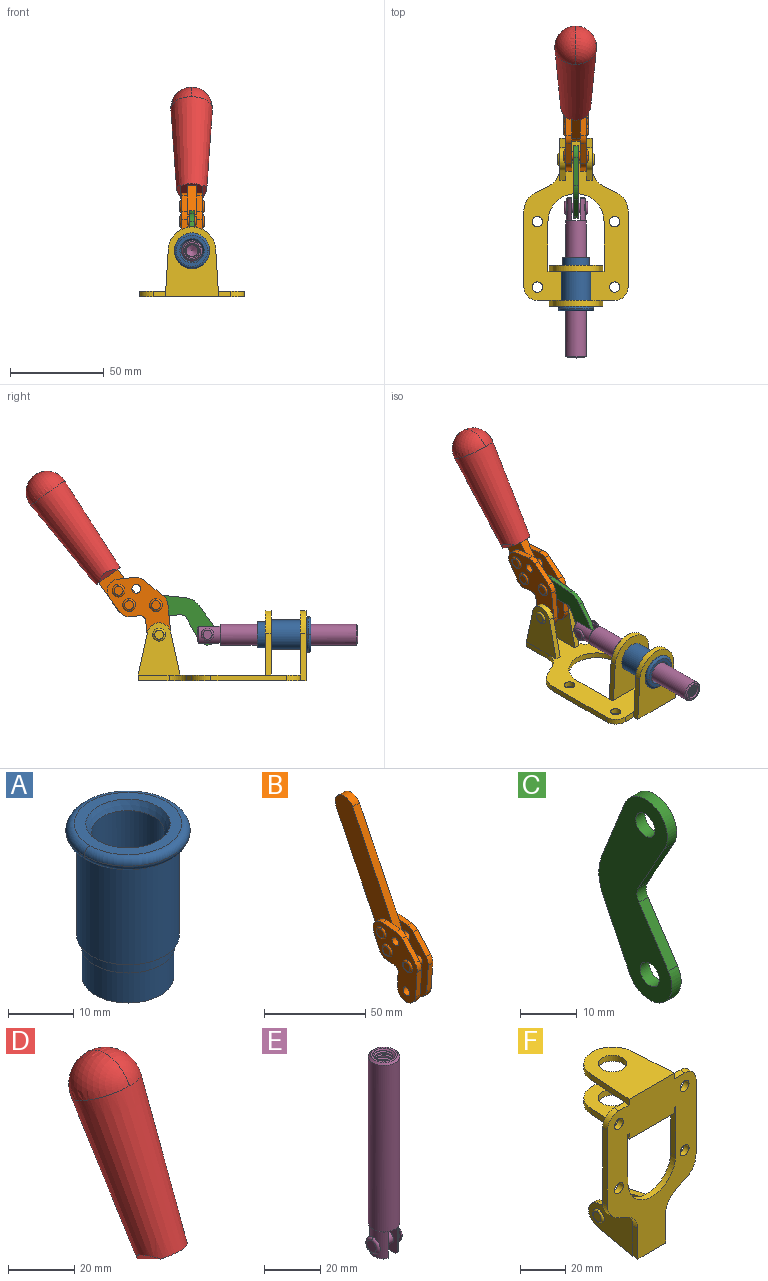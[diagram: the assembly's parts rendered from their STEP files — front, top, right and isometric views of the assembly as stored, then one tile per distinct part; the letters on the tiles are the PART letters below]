
ASSEMBLY  parts=6 mates=6
PART A: 15 faces, bbox 20.6x20.6x28.7 mm
  f0: torus R=8.26mm, axis (0,0,1), area 56.8mm2, adj f1,f10,f12
  f1: torus R=8.26mm, axis (0,0,1), area 56.8mm2, adj f0,f6,f13
  f2: cylinder r=5.59mm len=25.91mm, axis (0,0,1), area 909.6mm2, adj f3,f4
  f3: cone r=6.86mm half-angle=45deg, axis (0,0,-1), area 70.2mm2, adj f2,f14
  f4: cone r=6.47mm half-angle=30deg, axis (0,0,1), area 66.7mm2, adj f2,f13
  f5: cylinder r=7.04mm len=14.07mm, axis (0,0,1), area 252.6mm2, adj f11,f14
  f6: torus R=8.26mm, axis (0,0,1), area 56.8mm2, adj f1,f12,f13
  f7: cylinder r=7.16mm len=14.33mm, axis (0,0,1), area 91.5mm2, adj f9,f11
  f8: cylinder r=7.86mm len=18.42mm, axis (0,0,1), area 909.6mm2, adj f9,f10
  f9: plane 15.72x15.72mm, normal (0,0,-1), area 33mm2, adj f7,f8
  f10: plane 16.51x16.51mm, normal (0,0,-1), area 19.9mm2, adj f0,f8,f12
  f11: plane 14.33x14.33mm, normal (0,0,-1), area 5.7mm2, adj f5,f7
  f12: torus R=8.26mm, axis (0,0,1), area 56.8mm2, adj f0,f6,f10
  f13: plane 16.51x16.51mm, normal (0,0,1), area 82.7mm2, adj f1,f4,f6
  f14: plane 14.07x14.07mm, normal (0,0,-1), area 7.8mm2, adj f3,f5
PART B: 59 faces, bbox 12.9x60.2x99.6 mm
  f0: torus R=2.39mm, axis (-1,0,0), area 14.9mm2, adj f20,f43,f51
  f1: torus R=2.39mm, axis (-1,0,0), area 14.9mm2, adj f19,f42,f51
  f2: torus R=2.39mm, axis (-1,0,0), area 14.9mm2, adj f18,f35,f51
  f3: torus R=2.39mm, axis (-1,0,0), area 14.9mm2, adj f14,f17,f23
  f4: torus R=2.39mm, axis (-1,0,0), area 14.9mm2, adj f13,f16,f23
  f5: torus R=2.39mm, axis (-1,0,0), area 14.9mm2, adj f12,f15,f23
  f6: cylinder r=2.39mm len=4.78mm, axis (1,0,0), area 46.5mm2, adj f48,f50,f51
  f7: cylinder r=2.39mm len=4.78mm, axis (1,0,0), area 46.5mm2, adj f50,f51
  f8: cylinder r=6.35mm len=12.68mm, axis (1,0,0), area 61.8mm2, adj f38,f39,f50,f51
  f9: cylinder r=2.39mm len=4.78mm, axis (-1,0,0), area 70.5mm2, adj f46,f50
  f10: cylinder r=2.39mm len=4.78mm, axis (-1,0,0), area 46.5mm2, adj f23,f45,f46
  f11: cylinder r=2.39mm len=4.78mm, axis (-1,0,0), area 46.5mm2, adj f23,f46
  f12: plane 4.78x4.78mm, normal (1,0,0), area 17.9mm2, adj f5,f15
  f13: plane 4.78x4.78mm, normal (1,0,0), area 17.9mm2, adj f4,f16
  f14: plane 4.78x4.78mm, normal (1,0,0), area 17.9mm2, adj f3,f17
  f15: torus R=2.39mm, axis (-1,0,0), area 14.9mm2, adj f5,f12,f23
  f16: torus R=2.39mm, axis (-1,0,0), area 14.9mm2, adj f4,f13,f23
  f17: torus R=2.39mm, axis (-1,0,0), area 14.9mm2, adj f3,f14,f23
  f18: plane 4.78x4.78mm, normal (-1,0,0), area 17.9mm2, adj f2,f35
  f19: plane 4.78x4.78mm, normal (-1,0,0), area 17.9mm2, adj f1,f42
  f20: plane 4.78x4.78mm, normal (-1,0,0), area 17.9mm2, adj f0,f43
  f21: plane 2.26x0.2mm, normal (1,0,0), area 0.2mm2, adj f31,f44
  f22: plane 2.26x0.2mm, normal (-1,0,0), area 0.2mm2, adj f41,f44
  f23: plane 39.37x30.77mm, normal (1,0,0), area 565.5mm2, adj f3,f4,f5,f10,f11,f15,f16,f17
  f24: cylinder r=6.1mm len=4.15mm, axis (-1,0,0), area 14.7mm2, adj f23,f25,f32,f46
  f25: plane 10.25x9.01mm, normal (0,-0.75,0.66), area 42.3mm2, adj f23,f24,f26,f46
  f26: cylinder r=6.35mm len=4.64mm, axis (-1,0,0), area 15.6mm2, adj f23,f25,f27,f46
  f27: plane 15.84x3.1mm, normal (0,-1,-0.07), area 49.2mm2, adj f23,f26,f28,f46
  f28: cylinder r=6.35mm len=12.68mm, axis (-1,0,0), area 61.8mm2, adj f23,f27,f29,f46
  f29: plane 8.11x3.1mm, normal (0,1,0.07), area 25.2mm2, adj f23,f28,f30,f46
  f30: cylinder r=3.05mm len=3.25mm, axis (-1,0,0), area 14.8mm2, adj f23,f29,f31,f46
  f31: plane 5.99x3.1mm, normal (0,0.07,-1), area 18.6mm2, adj f21,f23,f30,f44,f46
  f32: plane 9.5x3.1mm, normal (0,-0.07,1), area 29.5mm2, adj f23,f24,f33,f46,f47
  f33: cylinder r=6.1mm len=8.63mm, axis (-1,0,0), area 39.1mm2, adj f23,f32,f34,f47
  f34: plane 8.65x3.96mm, normal (0,0.91,-0.42), area 29.5mm2, adj f23,f33,f44,f47
  f35: torus R=2.39mm, axis (-1,0,0), area 14.9mm2, adj f2,f18,f51
  f36: plane 10.25x9.01mm, normal (0,-0.75,0.66), area 42.3mm2, adj f37,f49,f50,f51
  f37: cylinder r=6.35mm len=4.64mm, axis (1,0,0), area 15.6mm2, adj f36,f38,f50,f51
  f38: plane 15.84x3.1mm, normal (0,-1,-0.07), area 49.2mm2, adj f8,f37,f50,f51
  f39: plane 8.11x3.1mm, normal (0,1,0.07), area 25.2mm2, adj f8,f40,f50,f51
  f40: cylinder r=3.05mm len=3.25mm, axis (1,0,0), area 14.8mm2, adj f39,f41,f50,f51
  f41: plane 5.99x3.1mm, normal (0,0.07,-1), area 18.6mm2, adj f22,f40,f44,f50,f51
  f42: torus R=2.39mm, axis (-1,0,0), area 14.9mm2, adj f1,f19,f51
  f43: torus R=2.39mm, axis (-1,0,0), area 14.9mm2, adj f0,f20,f51
  f44: cylinder r=6.35mm len=12.12mm, axis (-1,0,0), area 128.9mm2, adj f21,f22,f23,f31,f34,f41,f46,f47
  f45: plane 2.65x1.35mm, normal (1,0,0), area 1mm2, adj f10,f55
  f46: plane 39.08x20.42mm, normal (-1,0,0), area 412.5mm2, adj f9,f10,f11,f24,f25,f26,f27,f28
  f47: plane 77.62x39.82mm, normal (1,0,0), area 850mm2, adj f32,f33,f34,f44,f53,f54,f55
  f48: plane 2.65x1.35mm, normal (-1,0,0), area 1mm2, adj f6,f55
  f49: cylinder r=6.1mm len=4.15mm, axis (1,0,0), area 14.7mm2, adj f36,f50,f51,f56
  f50: plane 39.08x20.42mm, normal (1,0,0), area 412.5mm2, adj f6,f7,f8,f9,f36,f37,f38,f39
  f51: plane 39.37x30.77mm, normal (-1,0,0), area 565.5mm2, adj f0,f1,f2,f6,f7,f8,f35,f36
  f52: plane 8.65x3.96mm, normal (0,0.91,-0.42), area 29.5mm2, adj f44,f51,f57,f58
  f53: plane 68.49x33.4mm, normal (0,0.9,-0.44), area 358.1mm2, adj f44,f47,f54,f58
  f54: cylinder r=6.35mm len=12.06mm, axis (1,0,0), area 93.7mm2, adj f47,f53,f55,f58
  f55: plane 68.49x33.4mm, normal (0,-0.9,0.44), area 358.1mm2, adj f44,f45,f46,f47,f48,f50,f54,f58
  f56: plane 9.5x3.1mm, normal (0,-0.07,1), area 29.5mm2, adj f49,f50,f51,f57,f58
  f57: cylinder r=6.1mm len=8.63mm, axis (1,0,0), area 39.1mm2, adj f51,f52,f56,f58
  f58: plane 77.62x39.82mm, normal (-1,0,0), area 850mm2, adj f44,f52,f53,f54,f55,f56,f57
PART C: 12 faces, bbox 2.3x18.2x42.8 mm
  f0: cylinder r=2.4mm len=4.8mm, axis (1,0,0), area 34.9mm2, adj f4,f11
  f1: cylinder r=10.41mm len=8.47mm, axis (1,0,0), area 20.2mm2, adj f4,f9,f10,f11
  f2: cylinder r=3.05mm len=3.16mm, axis (1,0,0), area 7.7mm2, adj f4,f6,f7,f11
  f3: cylinder r=2.4mm len=4.8mm, axis (1,0,0), area 34.9mm2, adj f4,f11
  f4: plane 42.81x18.23mm, normal (-1,0,0), area 414.1mm2, adj f0,f1,f2,f3,f5,f6,f7,f8
  f5: cylinder r=5.54mm len=10.67mm, axis (1,0,0), area 41.8mm2, adj f4,f6,f10,f11
  f6: plane 11.66x6.53mm, normal (0,-0.87,-0.49), area 30.9mm2, adj f2,f4,f5,f11
  f7: plane 11.17x7.33mm, normal (0,-0.84,0.55), area 30.9mm2, adj f2,f4,f8,f11
  f8: cylinder r=5.54mm len=10.51mm, axis (1,0,0), area 41.8mm2, adj f4,f7,f9,f11
  f9: plane 13.67x6.67mm, normal (0,0.9,-0.44), area 35.1mm2, adj f1,f4,f8,f11
  f10: plane 14.1x5.7mm, normal (0,0.93,0.37), area 35.1mm2, adj f1,f4,f5,f11
  f11: plane 42.81x18.23mm, normal (1,0,0), area 414.1mm2, adj f0,f1,f2,f3,f5,f6,f7,f8
PART D: 11 faces, bbox 22.3x42.6x64.5 mm
  f0: sphere r=11.13mm, area 411.4mm2, adj f1,f8
  f1: cone r=11.11mm half-angle=3.3deg, axis (0,0.44,0.9), area 3251.8mm2, adj f0,f7,f8,f9,f10
  f2: cylinder r=6.16mm len=11.7mm, axis (1,0,0), area 89.5mm2, adj f3,f4,f5,f6
  f3: plane 60.23x36.75mm, normal (-1,0,0), area 763.6mm2, adj f2,f4,f6,f10
  f4: plane 51.37x25.05mm, normal (0,0.9,-0.44), area 264.2mm2, adj f2,f3,f5,f10
  f5: plane 60.23x36.75mm, normal (1,0,0), area 763.6mm2, adj f2,f4,f6,f10
  f6: plane 51.37x25.05mm, normal (0,-0.9,0.44), area 264.2mm2, adj f2,f3,f5,f10
  f7: plane 9.95x5.95mm, normal (0.71,-0.31,-0.64), area 25.8mm2, adj f1,f10
  f8: sphere r=11.13mm, area 411.4mm2, adj f0,f1
  f9: plane 9.95x5.95mm, normal (-0.71,-0.31,-0.64), area 25.8mm2, adj f1,f10
  f10: plane 14.27x11.38mm, normal (0,-0.44,-0.9), area 106.7mm2, adj f1,f3,f4,f5,f6,f7,f9
PART E: 48 faces, bbox 12.6x11.1x86.1 mm
  f0: torus R=2.41mm, axis (-1,0,0), area 15mm2, adj f30,f32,f34
  f1: torus R=2.41mm, axis (-1,0,0), area 15mm2, adj f29,f31,f33
  f2: cylinder r=5.54mm len=72.39mm, axis (0,0,1), area 2518.5mm2, adj f3,f4,f42,f43
  f3: cone r=5.54mm half-angle=45deg, axis (0,0,1), area 7.6mm2, adj f2,f5,f41
  f4: cone r=5.54mm half-angle=45deg, axis (0,0,-1), area 34.9mm2, adj f2,f39
  f5: cylinder r=5.08mm len=11.48mm, axis (0,0,1), area 108.3mm2, adj f3,f7,f8,f41
  f6: cylinder r=2.41mm len=4.83mm, axis (-1,0,0), area 71.2mm2, adj f40,f41
  f7: cylinder r=2.41mm len=4.83mm, axis (-1,0,0), area 7.6mm2, adj f5,f34
  f8: cone r=5.08mm half-angle=45deg, axis (0,0,1), area 10.6mm2, adj f5,f37,f41
  f9: cone r=3.98mm half-angle=45deg, axis (0,0,1), area 17.6mm2, adj f27,f39,f45,f46,f47
  f10: cylinder r=2.41mm len=4.83mm, axis (-1,0,0), area 7.6mm2, adj f33,f38
  f11: cylinder r=3.2mm len=6.4mm, axis (0,0,1), area 78.4mm2, adj f12,f28,f44,f45,f47
  f12: cylinder r=3.2mm len=6.4mm, axis (0,0,1), area 10.5mm2, adj f11,f13,f45,f47
  f13: cylinder r=3.2mm len=6.4mm, axis (0,0,1), area 10.5mm2, adj f12,f14,f45,f47
  f14: cylinder r=3.2mm len=6.4mm, axis (0,0,1), area 10.5mm2, adj f13,f15,f45,f47
  f15: cylinder r=3.2mm len=6.4mm, axis (0,0,1), area 10.5mm2, adj f14,f16,f45,f47
  f16: cylinder r=3.2mm len=6.4mm, axis (0,0,1), area 10.5mm2, adj f15,f17,f45,f47
  f17: cylinder r=3.2mm len=6.4mm, axis (0,0,1), area 10.5mm2, adj f16,f18,f45,f47
  f18: cylinder r=3.2mm len=6.4mm, axis (0,0,1), area 10.5mm2, adj f17,f19,f45,f47
  f19: cylinder r=3.2mm len=6.4mm, axis (0,0,1), area 10.5mm2, adj f18,f20,f45,f47
  f20: cylinder r=3.2mm len=6.4mm, axis (0,0,1), area 10.5mm2, adj f19,f21,f45,f47
  f21: cylinder r=3.2mm len=6.4mm, axis (0,0,1), area 10.5mm2, adj f20,f22,f45,f47
  f22: cylinder r=3.2mm len=6.4mm, axis (0,0,1), area 10.5mm2, adj f21,f23,f45,f47
  f23: cylinder r=3.2mm len=6.4mm, axis (0,0,1), area 10.5mm2, adj f22,f24,f45,f47
  f24: cylinder r=3.2mm len=6.4mm, axis (0,0,1), area 10.5mm2, adj f23,f25,f45,f47
  f25: cylinder r=3.2mm len=6.4mm, axis (0,0,1), area 10.5mm2, adj f24,f26,f45,f47
  f26: cylinder r=3.2mm len=6.4mm, axis (0,0,1), area 10.5mm2, adj f25,f27,f45,f47
  f27: cylinder r=3.2mm len=6.4mm, axis (0,0,1), area 7.4mm2, adj f9,f26,f45,f47
  f28: cone r=3.2mm half-angle=60deg, axis (0,0,1), area 37.2mm2, adj f11
  f29: plane 4.83x4.83mm, normal (-1,0,0), area 18.3mm2, adj f1,f31
  f30: plane 4.83x4.83mm, normal (1,0,0), area 18.3mm2, adj f0,f32
  f31: torus R=2.41mm, axis (-1,0,0), area 15mm2, adj f1,f29,f33
  f32: torus R=2.41mm, axis (-1,0,0), area 15mm2, adj f0,f30,f34
  f33: plane 6.83x6.83mm, normal (1,0,0), area 18.3mm2, adj f1,f10,f31
  f34: plane 6.83x6.83mm, normal (-1,0,0), area 18.3mm2, adj f0,f7,f32
  f35: cone r=5.08mm half-angle=45deg, axis (0,0,1), area 10.6mm2, adj f36,f38,f40
  f36: plane 7.25x1.97mm, normal (0,0,-1), area 10mm2, adj f35,f40
  f37: plane 7.25x1.97mm, normal (0,0,-1), area 10mm2, adj f8,f41
  f38: cylinder r=5.08mm len=11.48mm, axis (0,0,1), area 108.3mm2, adj f10,f35,f40,f42
  f39: plane 9.55x9.55mm, normal (0,0,1), area 22mm2, adj f4,f9
  f40: plane 12.76x10.09mm, normal (1,0,0), area 95.7mm2, adj f6,f35,f36,f38,f42,f43
  f41: plane 12.76x10.09mm, normal (-1,0,0), area 95.7mm2, adj f3,f5,f6,f8,f37,f43
  f42: cone r=5.54mm half-angle=45deg, axis (0,0,1), area 7.6mm2, adj f2,f38,f40
  f43: plane 11.07x4.7mm, normal (0,0,-1), area 50.4mm2, adj f2,f40,f41
  f44: plane 0.89x0.62mm, normal (-1,0,0), area 0.3mm2, adj f11,f45,f46,f47
  f45: bspline ~24.8x7.63mm, area 266.6mm2, adj f9,f11,f12,f13,f14,f15,f16,f17
  f46: bspline ~24.87x7.63mm, area 73.6mm2, adj f9,f44,f45,f47
  f47: bspline ~24.98x7.63mm, area 272.5mm2, adj f9,f11,f12,f13,f14,f15,f16,f17
PART F: 55 faces, bbox 55.7x37.4x89.8 mm
  f0: torus R=2.41mm, axis (-1,0,0), area 15mm2, adj f11,f15,f25
  f1: torus R=2.41mm, axis (-1,0,0), area 15mm2, adj f10,f12,f22
  f2: cylinder r=2.78mm len=5.56mm, axis (0,-1,0), area 54.2mm2, adj f30,f54
  f3: cylinder r=14.99mm len=29.97mm, axis (0,-1,0), area 145.9mm2, adj f30,f49,f53,f54
  f4: cylinder r=2.78mm len=5.56mm, axis (0,-1,0), area 54.2mm2, adj f30,f54
  f5: cylinder r=2.78mm len=5.56mm, axis (0,-1,0), area 54.2mm2, adj f30,f54
  f6: cylinder r=2.78mm len=5.56mm, axis (0,-1,0), area 54.2mm2, adj f30,f54
  f7: cylinder r=6.35mm len=12.7mm, axis (0,0,1), area 123.6mm2, adj f27,f51
  f8: cylinder r=6.35mm len=12.7mm, axis (0,0,-1), area 124.7mm2, adj f21,f35
  f9: cylinder r=2.41mm len=11.18mm, axis (-1,0,0), area 169.4mm2, adj f16,f19
  f10: plane 4.83x4.83mm, normal (1,0,0), area 18.3mm2, adj f1,f12
  f11: plane 4.83x4.83mm, normal (-1,0,0), area 18.3mm2, adj f0,f15
  f12: torus R=2.41mm, axis (-1,0,0), area 15mm2, adj f1,f10,f22
  f13: cylinder r=6.35mm len=12.41mm, axis (1,0,0), area 53.4mm2, adj f18,f19,f22,f23
  f14: cylinder r=6.35mm len=12.41mm, axis (-1,0,0), area 53.4mm2, adj f16,f17,f24,f25
  f15: torus R=2.41mm, axis (-1,0,0), area 15mm2, adj f0,f11,f25
  f16: plane 27.86x22.35mm, normal (1,0,0), area 425.4mm2, adj f9,f14,f17,f24,f30
  f17: plane 22.86x4.97mm, normal (0,0.21,0.98), area 72.5mm2, adj f14,f16,f25,f30
  f18: plane 22.86x4.97mm, normal (0,0.21,0.98), area 72.5mm2, adj f13,f19,f22,f30
  f19: plane 27.86x22.35mm, normal (-1,0,0), area 425.4mm2, adj f9,f13,f18,f23,f30
  f20: cylinder r=12.7mm len=25.35mm, axis (0,0,-1), area 119.8mm2, adj f21,f34,f35,f36
  f21: plane 34.21x28.07mm, normal (0,0,-1), area 702.4mm2, adj f8,f20,f30,f34,f36
  f22: plane 27.96x22.45mm, normal (1,0,0), area 407.2mm2, adj f1,f12,f13,f18,f23,f30,f42,f43
  f23: plane 22.86x4.97mm, normal (0,0.21,-0.98), area 72.5mm2, adj f13,f19,f22,f44
  f24: plane 22.86x4.97mm, normal (0,0.21,-0.98), area 72.5mm2, adj f14,f16,f25,f44
  f25: plane 27.86x22.35mm, normal (-1,0,0), area 407.1mm2, adj f0,f14,f15,f17,f24,f30,f45,f46
  f26: plane 3.1x0.95mm, normal (0,0,-1), area 2.7mm2, adj f30,f49,f50,f54
  f27: plane 34.21x28.07mm, normal (0,0,1), area 702.4mm2, adj f7,f28,f30,f50,f52
  f28: cylinder r=12.7mm len=25.35mm, axis (0,0,1), area 118.8mm2, adj f27,f50,f51,f52
  f29: plane 3.1x0.95mm, normal (0,0,-1), area 2.7mm2, adj f30,f52,f53,f54
  f30: plane 86.54x55.63mm, normal (0,1,0), area 2362.9mm2, adj f2,f3,f4,f5,f6,f16,f17,f18
  f31: plane 40.56x3.1mm, normal (-1,0,0), area 125.7mm2, adj f30,f32,f48,f54
  f32: cylinder r=7.11mm len=7.11mm, axis (0,-1,0), area 34.6mm2, adj f30,f31,f33,f54
  f33: plane 6.67x3.1mm, normal (0,0,1), area 20.4mm2, adj f30,f32,f34,f54
  f34: plane 25.39x3.13mm, normal (-1,0.06,0), area 79.5mm2, adj f20,f21,f33,f35,f54
  f35: plane 37.31x28.45mm, normal (0,0,1), area 789.9mm2, adj f8,f20,f34,f36,f54
  f36: plane 25.39x3.13mm, normal (1,0.06,0), area 79.5mm2, adj f20,f21,f35,f37,f54
  f37: plane 6.67x3.1mm, normal (0,0,1), area 20.4mm2, adj f30,f36,f38,f54
  f38: cylinder r=7.11mm len=7.11mm, axis (0,-1,0), area 34.6mm2, adj f30,f37,f39,f54
  f39: plane 40.56x3.1mm, normal (1,0,0), area 125.7mm2, adj f30,f38,f40,f54
  f40: cylinder r=11.18mm len=10.16mm, axis (0,-1,0), area 39.5mm2, adj f30,f39,f41,f54
  f41: plane 6.09x3.1mm, normal (0.42,0,-0.91), area 20.8mm2, adj f30,f40,f42,f54
  f42: cylinder r=11.18mm len=9.41mm, axis (0,-1,0), area 37.2mm2, adj f22,f30,f41,f43,f54
  f43: plane 16.5x3.1mm, normal (1,0,0), area 51.1mm2, adj f22,f42,f44,f54
  f44: plane 17.37x3.1mm, normal (0,0,-1), area 53.8mm2, adj f23,f24,f30,f43,f45,f54
  f45: plane 16.5x3.1mm, normal (-1,0,0), area 51.1mm2, adj f25,f44,f46,f54
  f46: cylinder r=11.18mm len=9.41mm, axis (0,-1,0), area 37.2mm2, adj f25,f30,f45,f47,f54
  f47: plane 6.09x3.1mm, normal (-0.42,0,-0.91), area 20.8mm2, adj f30,f46,f48,f54
  f48: cylinder r=11.18mm len=10.16mm, axis (0,-1,0), area 39.5mm2, adj f30,f31,f47,f54
  f49: plane 26.54x3.1mm, normal (-1,0,0), area 82.3mm2, adj f3,f26,f30,f54
  f50: plane 25.39x3.1mm, normal (1,0.06,0), area 78.8mm2, adj f26,f27,f28,f51,f54
  f51: plane 37.31x28.45mm, normal (0,0,-1), area 789.9mm2, adj f7,f28,f50,f52,f54
  f52: plane 25.39x3.1mm, normal (-1,0.06,0), area 78.8mm2, adj f27,f28,f29,f51,f54
  f53: plane 26.54x3.1mm, normal (1,0,0), area 82.3mm2, adj f3,f29,f30,f54
  f54: plane 89.66x55.63mm, normal (0,-1,0), area 2678.5mm2, adj f2,f3,f4,f5,f6,f26,f29,f31
PLACE A rot(axis=(1,0,0),90deg) t=(0,9.43,0)mm
PLACE B rot(axis=(-1,0,0),10deg) t=(0,22.86,60.49)mm
PLACE C rot(axis=(1,0,0),121.8deg) t=(0,41.76,11.86)mm
PLACE D rot(axis=(-1,0,0),10deg) t=(-0.19,22.86,60.49)mm
PLACE E rot(axis=(1,0,0),90deg) t=(0,31.11,0)mm
PLACE F rot(axis=(1,0,0),90deg) t=(0,9.43,0)mm fixed
MATE revolute F.f0 <-> B.f7  axis (-1,0,0) through (0,41.52,24.61)mm
MATE fastened D.f2 <-> B.f54  axis (1,0,0) through (-2.5,102.33,102.1)mm
MATE revolute C.f5 <-> E.f6  axis (1,0,0) through (0,15.64,24.61)mm
MATE slider E.f2 <-> F.f7  axis (0,-1,0) through (0,-27.67,24.61)mm
MATE revolute C.f3 <-> B.f4  axis (1,0,0) through (0,43.18,40.4)mm
MATE fastened A.f0 <-> F.f7  axis (0,-1,0) through (0,-36.96,24.61)mm
